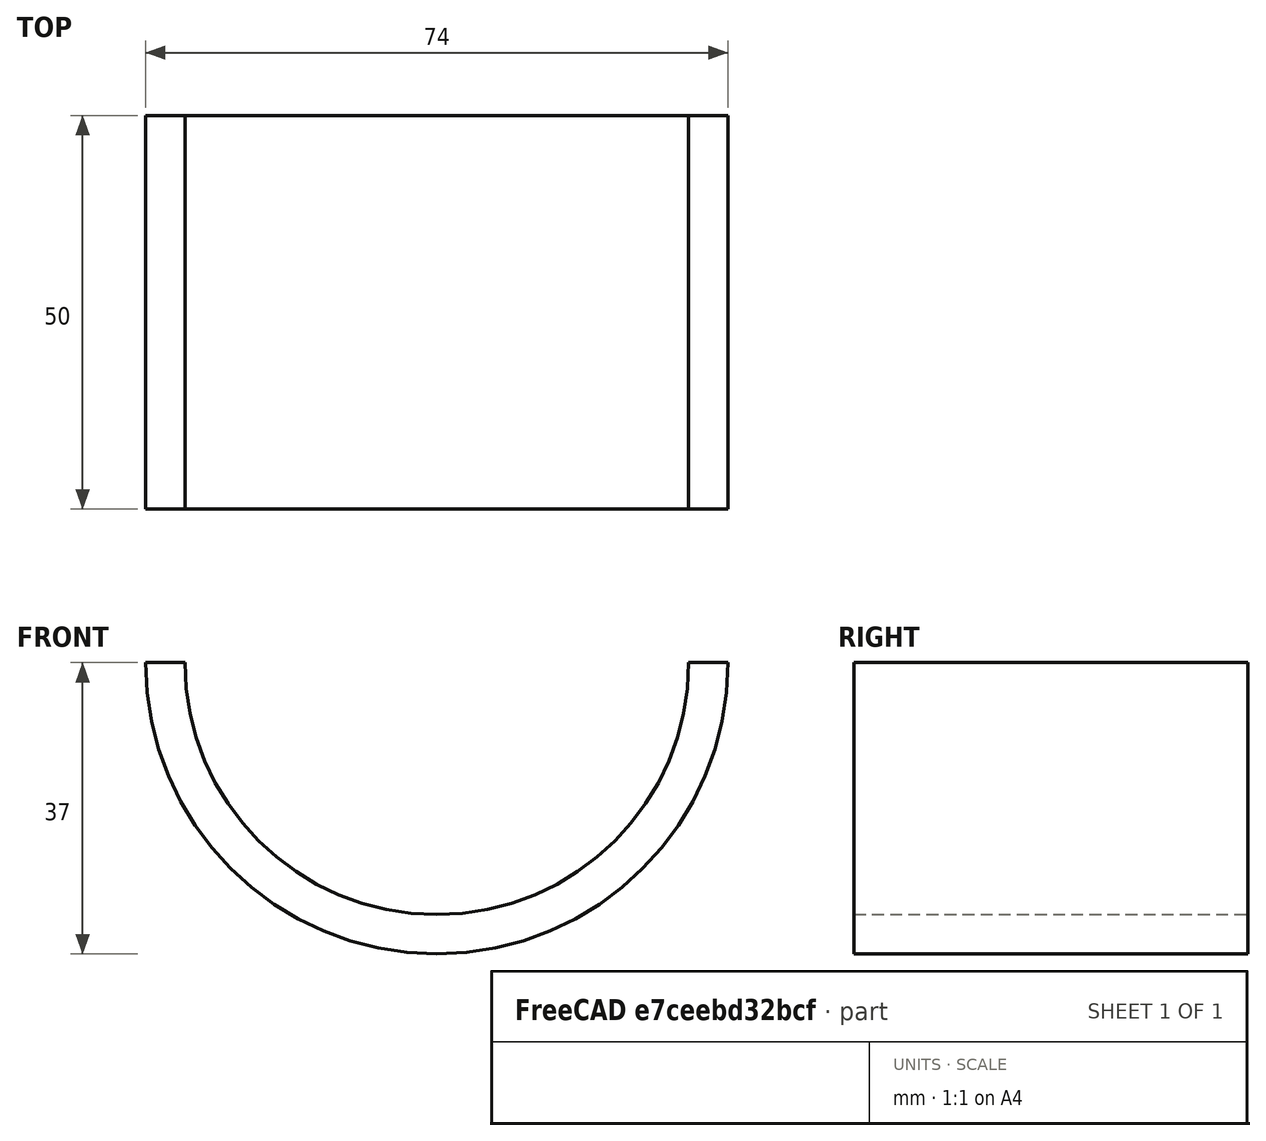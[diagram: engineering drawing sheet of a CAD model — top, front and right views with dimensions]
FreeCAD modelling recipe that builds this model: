
FCSTD DOCUMENT  (FreeCAD 1.0R38806 (Git))
Label: simplified
License: All rights reserved
LicenseURL: https://en.wikipedia.org/wiki/All_rights_reserved
objects: Sketcher::SketchObject×1, PartDesign::Pad×1, PartDesign::Body×1
note: 6 computed .brp shape members not serialized (recipe doc carries the construction recipe); baked Part::Feature solids carry a one-line shape summary decoded from their .brp

FEATURE [Sketcher::SketchObject] Sketch
  ArcFitTolerance = 1e-06
  AttachmentSupport = -> [XZ_Plane]
  FullyConstrained = true
  MakeInternals = false
  MapMode = 5
  Placement = pos=(0,0,0) rot=(1,0,0;1.5708rad)
  sketch-geometry (4):
    g0: ArcOfCircle CenterX=0 CenterY=0 CenterZ=0 NormalX=0 NormalY=0 NormalZ=1 AngleXU=0 Radius=37 StartAngle=3.14159 EndAngle=6.28319
    g1: ArcOfCircle CenterX=0 CenterY=0 CenterZ=0 NormalX=0 NormalY=0 NormalZ=1 AngleXU=0 Radius=32 StartAngle=3.14159 EndAngle=6.28319
    g2: LineSegment StartX=-37 StartY=0 StartZ=0 EndX=-32 EndY=3.9e-15 EndZ=0
    g3: LineSegment StartX=32 StartY=-7.8e-15 StartZ=0 EndX=37 EndY=-9.1e-15 EndZ=0
  constraints (12):
    c: Coincident(g0,g-1)
    c: PointOnObject(g0,g-1)
    c: PointOnObject(g0,g-1)
    c: Radius(g0) = 37
    c: Coincident(g1,g0)
    c: PointOnObject(g1,g-1)
    c: PointOnObject(g1,g-1)
    c: Distance(g1,g0) = 5
    c: Coincident(g2,g0)
    c: Coincident(g2,g1)
    c: Coincident(g3,g1)
    c: Coincident(g3,g0)
FEATURE [PartDesign::Pad] Pad
  Direction = (0,-1,2e-16)
  Length = 50
  Length2 = 10
  Placement = pos=(0,0,0) rot=(1,0,0;1.5708rad)
  Profile = -> Sketch
  ReferenceAxis = -> Sketch [N_Axis]
  Refine = true
  Suppressed = false
  Type = 0
FEATURE [PartDesign::Body] Body
  AllowCompound = false
  Group = -> [Sketch,Pad]
  Origin = -> Origin
  Tip = -> Pad
